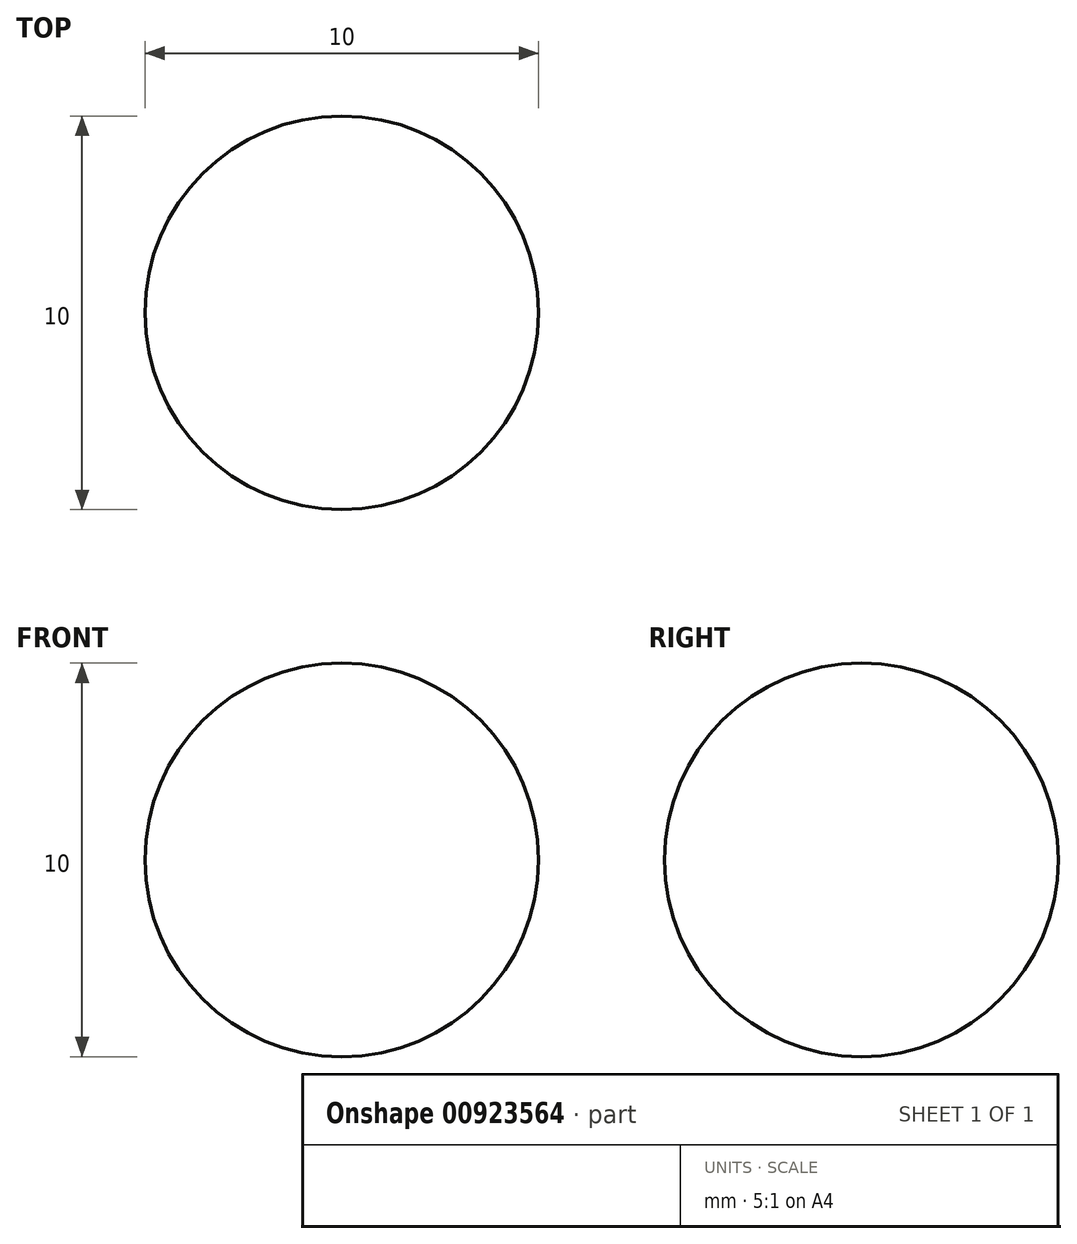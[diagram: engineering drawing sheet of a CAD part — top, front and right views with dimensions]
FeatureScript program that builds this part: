
annotation { "Feature Type Name" : "Feature", "Feature Type Description" : "" }
export const myFeature = defineFeature(function(context is Context, id is Id, definition is map)
    precondition{}
    {
        {
            var Q0;
            Q0=qCreatedBy(makeId("Front.planeOp"),FACE);
            var sketch = newSketch(context, id + "F0", { "sketchPlane" : qUnion([Q0])});
            skCircle(sketch, "E0", {"center": v(0, 0) * mm, "radius": 27.5 * mm, "construction": true});
            skLineSegment(sketch, "E1", {"start": v(-27.5, 0) * mm, "end": v(27.5, 0) * mm, "construction": true});
            skArc(sketch, "E2", {"start": v(0, 32.5) * mm, "mid": v(-5, 27.5) * mm, "end": v(0, 22.5) * mm});
            skLineSegment(sketch, "E3", {"start": v(0, 32.5) * mm, "end": v(0, 22.5) * mm});
            skSolve(sketch);
        }
        {
            var Q0;
            Q0=makeQuery(id+"F0.imprint","IMPRINT",FACE,{"disambiguationData":[TD([[makeQuery(id+"F0.imprint","IMPRINT",EDGE,{"derivedFrom":sQuery(id+"F0.wireOp",EDGE,"E2")}),1.0]])]});
            var Q1;
            Q1=sQuery(id+"F0.wireOp",EDGE,"E3");
            revolve(context, id + "F1", {"surfaceOperationType" : NewSurfaceOperationType.NEW, "entities" : qUnion([Q0]), "axis" : qUnion([Q1]), "revolveType" : RevolveType.FULL});
        }
        {
            var Q0;
            Q0=qCreatedBy(makeId("Front.planeOp"),FACE);
            var sketch = newSketch(context, id + "F2", { "sketchPlane" : qUnion([Q0])});
            skLineSegment(sketch, "E4", {"start": v(0, 0) * mm, "end": v(50, 0) * mm, "construction": true});
            skSolve(sketch);
        }
    });
